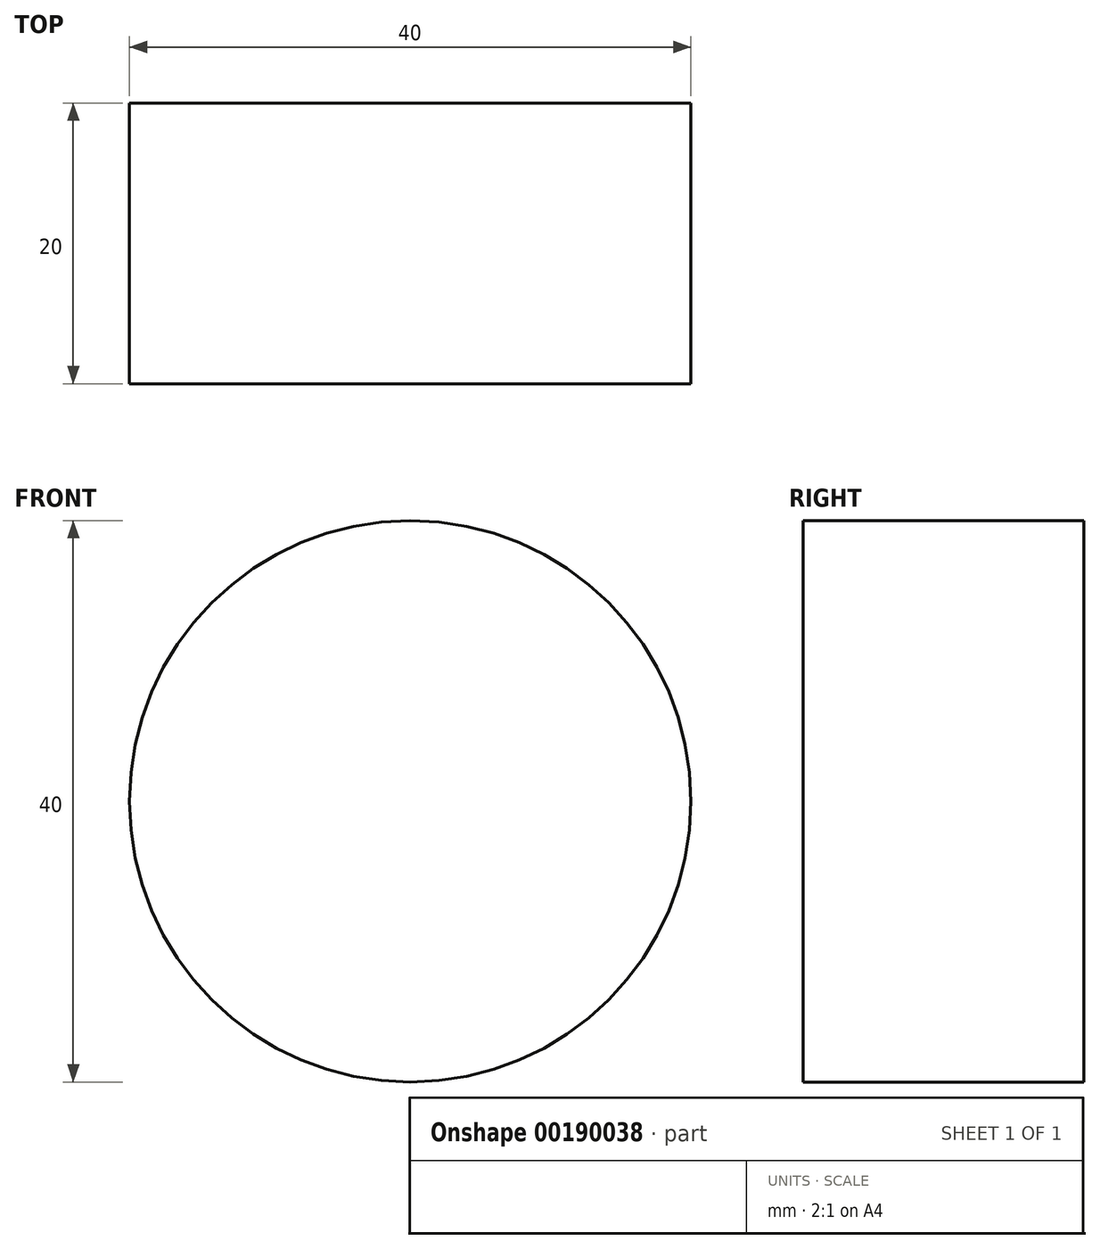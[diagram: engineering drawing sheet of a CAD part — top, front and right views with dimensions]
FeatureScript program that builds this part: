
annotation { "Feature Type Name" : "Feature", "Feature Type Description" : "" }
export const myFeature = defineFeature(function(context is Context, id is Id, definition is map)
    precondition{}
    {
        {
            var Q0;
            Q0=qCreatedBy(makeId("Top.planeOp"),FACE);
            var sketch = newSketch(context, id + "F0", { "sketchPlane" : qUnion([Q0])});
            skLineSegment(sketch, "E0", {"start": v(-9.36, 22.15) * mm, "end": v(-29.36, 22.15) * mm});
            skLineSegment(sketch, "E1", {"start": v(-29.36, 22.15) * mm, "end": v(-29.36, 2.15) * mm});
            skLineSegment(sketch, "E2", {"start": v(-29.36, 2.15) * mm, "end": v(-9.36, 2.15) * mm});
            skLineSegment(sketch, "E3", {"start": v(-9.36, 2.15) * mm, "end": v(-9.36, 22.15) * mm});
            skSolve(sketch);
        }
        {
            var Q0;
            Q0 = qSketchRegion(id + "F0", true);
            var Q1;
            Q1=sQuery(id+"F0.wireOp",EDGE,"E3");
            revolve(context, id + "F1", {"entities" : qUnion([Q0]), "axis" : qUnion([Q1]), "revolveType" : RevolveType.FULL});
        }
    });
